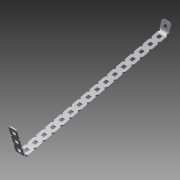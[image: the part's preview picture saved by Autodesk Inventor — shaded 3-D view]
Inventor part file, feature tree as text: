
AUTODESK INVENTOR PART (.ipt)
format: ipt  version: 2012 (Build 160160000, 160)  size: 914,432 bytes
history: native  units: in
note: dims shown in document units (in); Inventor stores cm internally (conversion verified against a paired STEP export)
features: other x4, sketch x3, imported_body x1, plane x1, split x1
ambient origin geometry x8: Origin, YZ Plane, XZ Plane, XY Plane, X Axis, Y Axis, Z Axis, Center Point
feature tree (10):
  parser-record x1  (decoder bookkeeping rows leaked as tree rows — omitted from the tree; the rows remain in map.json)
  imported_body  "Base1"
  plane  "Work Plane1"
  split  "Split1"
  other  "Bend Part1"
  other  "Bend Part3"
  other  "Bend Part4"
  sketch  "Sketch1"  dims[d0=-2.5in]
  sketch  "Sketch3"  dims[d1=0.12in d2=0.5978in]
  sketch  "Sketch4"  dims[d5=0.25in d6=45.0deg d7=0.25in d8=60.0deg]
